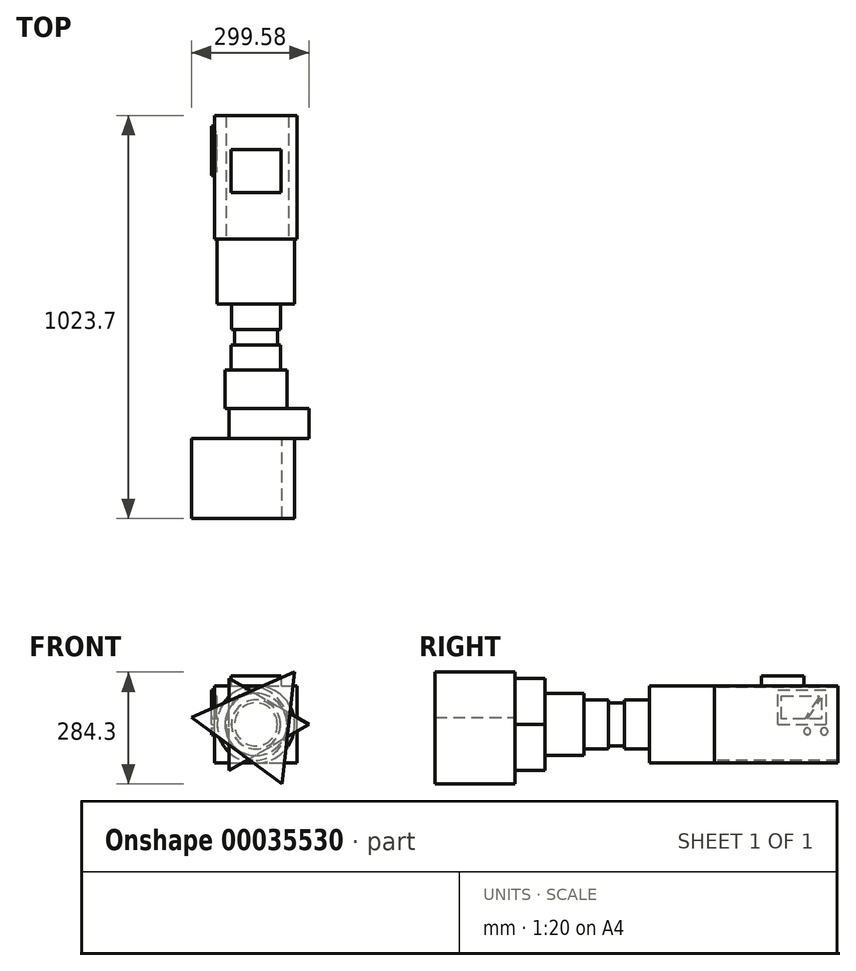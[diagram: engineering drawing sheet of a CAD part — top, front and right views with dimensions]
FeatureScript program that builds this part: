
annotation { "Feature Type Name" : "Feature", "Feature Type Description" : "" }
export const myFeature = defineFeature(function(context is Context, id is Id, definition is map)
    precondition{}
    {
        {
            var Q0;
            Q0=qCreatedBy(makeId("Front.planeOp"),FACE);
            var sketch = newSketch(context, id + "F0", { "sketchPlane" : qUnion([Q0])});
            skCircle(sketch, "E0", {"center": v(0, 0) * mm, "radius": 62.51 * mm});
            skSolve(sketch);
        }
        {
            var Q0;
            Q0=makeQuery(id+"F0.imprint","IMPRINT",FACE,{"disambiguationData":[TD([[makeQuery(id+"F0.imprint","IMPRINT",EDGE,{"derivedFrom":sQuery(id+"F0.wireOp",EDGE,"E0")}),1.0]])]});
            extrude(context, id + "F1", {"entities" : qUnion([Q0]), "depth" : 93.62 * mm, "hasSecondDirection" : true, "secondDirectionOppositeDirection" : true, "secondDirectionDepth" : 67.67 * mm});
        }
        {
            var Q0;
            Q0=makeQuery(id+"F1.opExtrude","CAP_FACE",FACE,{"disambiguationData":[OSD([sQuery(id+"F0.wireOp",EDGE,"E0")])],"isStart":false});
            var sketch = newSketch(context, id + "F2", { "sketchPlane" : qUnion([Q0])});
            skCircle(sketch, "E1", {"center": v(0, 0) * mm, "radius": 78.95 * mm});
            skSolve(sketch);
        }
        {
            var Q0;
            Q0 = qSketchRegion(id + "F2", true);
            extrude(context, id + "F3", {"entities" : qUnion([Q0]), "operationType" : NewBodyOperationType.ADD, "oppositeDirection" : true, "depth" : 97.99 * mm});
        }
        {
            var Q0;
            Q0=makeQuery(id+"F1.opExtrude","CAP_FACE",FACE,{"disambiguationData":[OSD([sQuery(id+"F0.wireOp",EDGE,"E0")])],"isStart":true});
            var sketch = newSketch(context, id + "F4", { "sketchPlane" : qUnion([Q0])});
            skCircle(sketch, "E2", {"center": v(0, 0) * mm, "radius": 54.56 * mm});
            skSolve(sketch);
        }
        {
            var Q0;
            Q0 = qSketchRegion(id + "F4", true);
            extrude(context, id + "F5", {"entities" : qUnion([Q0]), "operationType" : NewBodyOperationType.ADD, "depth" : 40.02 * mm});
        }
        {
            var Q0;
            Q0=makeQuery(id+"F5.opExtrude","CAP_FACE",FACE,{"disambiguationData":[OSD([sQuery(id+"F4.wireOp",EDGE,"E2")])],"isStart":false});
            var sketch = newSketch(context, id + "F6", { "sketchPlane" : qUnion([Q0])});
            skCircle(sketch, "E3", {"center": v(0, 0) * mm, "radius": 62.09 * mm});
            skSolve(sketch);
        }
        {
            var Q0;
            Q0 = qSketchRegion(id + "F6", true);
            extrude(context, id + "F7", {"entities" : qUnion([Q0]), "operationType" : NewBodyOperationType.ADD, "depth" : 64.06 * mm});
        }
        {
            var Q0;
            Q0=makeQuery(id+"F7.opExtrude","CAP_FACE",FACE,{"disambiguationData":[OSD([sQuery(id+"F6.wireOp",EDGE,"E3")])],"isStart":false});
            var sketch = newSketch(context, id + "F8", { "sketchPlane" : qUnion([Q0])});
            skCircle(sketch, "E4", {"center": v(0, 0) * mm, "radius": 98.34 * mm});
            skSolve(sketch);
        }
        {
            var Q0;
            Q0 = qSketchRegion(id + "F8", true);
            extrude(context, id + "F9", {"entities" : qUnion([Q0]), "operationType" : NewBodyOperationType.ADD, "depth" : 164.96 * mm});
        }
        {
            var Q0;
            Q0=makeQuery(id+"F9.opExtrude","CAP_FACE",FACE,{"disambiguationData":[OSD([sQuery(id+"F8.wireOp",EDGE,"E4")])],"isStart":false});
            var sketch = newSketch(context, id + "F10", { "sketchPlane" : qUnion([Q0])});
            skLineSegment(sketch, "E5.bottom", {"start": v(0, 0) * mm, "end": v(-104.59, 0) * mm});
            skLineSegment(sketch, "E5.top", {"start": v(0, 98.34) * mm, "end": v(-104.59, 98.34) * mm});
            skLineSegment(sketch, "E5.left", {"start": v(0, 0) * mm, "end": v(0, 98.34) * mm});
            skLineSegment(sketch, "E5.right", {"start": v(-104.59, 0) * mm, "end": v(-104.59, 98.34) * mm});
            skLineSegment(sketch, "E6.MirrorCS", {"start": v(0, 98.34) * mm, "end": v(104.59, 98.34) * mm});
            skLineSegment(sketch, "E7.MirrorCS", {"start": v(104.59, 0) * mm, "end": v(104.59, 98.34) * mm});
            skLineSegment(sketch, "E8.MirrorCS", {"start": v(0, 0) * mm, "end": v(104.59, 0) * mm});
            skLineSegment(sketch, "E9.MirrorCS", {"start": v(-104.59, 0) * mm, "end": v(-104.59, -98.34) * mm});
            skLineSegment(sketch, "E10.MirrorCS", {"start": v(0, -98.34) * mm, "end": v(-104.59, -98.34) * mm});
            skLineSegment(sketch, "E11.MirrorCS", {"start": v(0, 0) * mm, "end": v(0, -98.34) * mm});
            skLineSegment(sketch, "E12.MirrorCS", {"start": v(0, -98.34) * mm, "end": v(104.59, -98.34) * mm});
            skLineSegment(sketch, "E13.MirrorCS", {"start": v(104.59, 0) * mm, "end": v(104.59, -98.34) * mm});
            skFitSpline(sketch, "E14", {"points": [v(-83.55, 0) * mm, v(0, 94.29) * mm, v(75.89, 0) * mm, v(0, -91.4) * mm, v(-83.55, 0) * mm]});
            skSolve(sketch);
        }
        {
            var Q0;
            Q0 = qSketchRegion(id + "F10", true);
            extrude(context, id + "F11", {"entities" : qUnion([Q0]), "operationType" : NewBodyOperationType.ADD, "depth" : 313.97 * mm});
        }
        {
            var Q0;
            Q0=makeQuery(id+"F11.opExtrude","SWEPT_FACE",FACE,{"disambiguationData":[OSD([sQuery(id+"F10.wireOp",EDGE,"E5.top"),sQuery(id+"F10.wireOp",EDGE,"E6.MirrorCS")])]});
            var sketch = newSketch(context, id + "F12", { "sketchPlane" : qUnion([Q0])});
            skCircle(sketch, "E15.cCircle", {"center": v(0, 509.8) * mm, "radius": 87.57 * mm, "construction": true});
            skLineSegment(sketch, "E15.0", {"start": v(-86.16, 562.73) * mm, "end": v(2.77, 610.88) * mm});
            skLineSegment(sketch, "E15.1", {"start": v(2.77, 610.88) * mm, "end": v(88.92, 557.94) * mm});
            skLineSegment(sketch, "E15.2", {"start": v(88.92, 557.94) * mm, "end": v(86.16, 456.86) * mm});
            skLineSegment(sketch, "E15.3", {"start": v(86.16, 456.86) * mm, "end": v(-2.77, 408.7) * mm});
            skLineSegment(sketch, "E15.4", {"start": v(-2.77, 408.7) * mm, "end": v(-88.92, 461.64) * mm});
            skLineSegment(sketch, "E15.5", {"start": v(-88.92, 461.64) * mm, "end": v(-86.16, 562.73) * mm});
            skPoint(sketch, "E15.0.midPoint", {"position": v(-41.7, 586.8) * mm});
            skLineSegment(sketch, "E16.bottom", {"start": v(0, 509.8) * mm, "end": v(63.62, 509.8) * mm});
            skLineSegment(sketch, "E16.top", {"start": v(0, 564.12) * mm, "end": v(63.62, 564.12) * mm});
            skLineSegment(sketch, "E16.left", {"start": v(0, 509.8) * mm, "end": v(0, 564.12) * mm});
            skLineSegment(sketch, "E16.right", {"start": v(63.62, 509.8) * mm, "end": v(63.62, 564.12) * mm});
            skLineSegment(sketch, "E17.MirrorCS", {"start": v(0, 564.12) * mm, "end": v(-63.62, 564.12) * mm});
            skLineSegment(sketch, "E18.MirrorCS", {"start": v(-63.62, 509.8) * mm, "end": v(-63.62, 564.12) * mm});
            skLineSegment(sketch, "E19.MirrorCS", {"start": v(0, 509.8) * mm, "end": v(-63.62, 509.8) * mm});
            skLineSegment(sketch, "E20.MirrorCS", {"start": v(63.62, 509.8) * mm, "end": v(63.62, 455.46) * mm});
            skLineSegment(sketch, "E21.MirrorCS", {"start": v(0, 455.46) * mm, "end": v(63.62, 455.46) * mm});
            skLineSegment(sketch, "E22.MirrorCS", {"start": v(0, 509.8) * mm, "end": v(0, 455.46) * mm});
            skLineSegment(sketch, "E23.MirrorCS", {"start": v(-63.62, 509.8) * mm, "end": v(-63.62, 455.46) * mm});
            skLineSegment(sketch, "E24.MirrorCS", {"start": v(0, 455.46) * mm, "end": v(-63.62, 455.46) * mm});
            skSolve(sketch);
        }
        {
            var Q0;
            Q0=makeQuery(id+"F12.imprint","IMPRINT",FACE,{"disambiguationData":[TD([[makeQuery(id+"F12.imprint","IMPRINT",EDGE,{"derivedFrom":sQuery(id+"F12.wireOp",EDGE,"E16.bottom")}),1.0]])]});
            var Q1;
            Q1=makeQuery(id+"F12.imprint","IMPRINT",FACE,{"disambiguationData":[TD([[makeQuery(id+"F12.imprint","IMPRINT",EDGE,{"derivedFrom":sQuery(id+"F12.wireOp",EDGE,"E16.left")}),1.0]])]});
            var Q2;
            Q2=makeQuery(id+"F12.imprint","IMPRINT",FACE,{"disambiguationData":[TD([[makeQuery(id+"F12.imprint","IMPRINT",EDGE,{"derivedFrom":sQuery(id+"F12.wireOp",EDGE,"E16.bottom")}),-1.0]])]});
            var Q3;
            Q3=makeQuery(id+"F12.imprint","IMPRINT",FACE,{"disambiguationData":[TD([[makeQuery(id+"F12.imprint","IMPRINT",EDGE,{"derivedFrom":sQuery(id+"F12.wireOp",EDGE,"E22.MirrorCS")}),-1.0]])]});
            extrude(context, id + "F13", {"entities" : qUnion([Q0, Q1, Q2, Q3]), "operationType" : NewBodyOperationType.ADD, "depth" : 25.4 * mm});
        }
        {
            var Q0;
            Q0=makeQuery(id+"F3.boolean.opBoolean","MERGE",FACE,{"derivedFrom":[makeQuery(id+"F1.opExtrude","CAP_FACE",FACE,{"disambiguationData":[OSD([sQuery(id+"F0.wireOp",EDGE,"E0")])],"isStart":false}),makeQuery(id+"F3.opExtrude","CAP_FACE",FACE,{"disambiguationData":[OSD([sQuery(id+"F2.wireOp",EDGE,"E1")])],"isStart":true})]});
            var sketch = newSketch(context, id + "F14", { "sketchPlane" : qUnion([Q0])});
            skCircle(sketch, "E25.cCircle", {"center": v(0, 0) * mm, "radius": 67.72 * mm, "construction": true});
            skLineSegment(sketch, "E25.0", {"start": v(-67.72, -117.3) * mm, "end": v(-67.72, 117.3) * mm});
            skLineSegment(sketch, "E25.1", {"start": v(-67.72, 117.3) * mm, "end": v(135.44, 0) * mm});
            skLineSegment(sketch, "E25.2", {"start": v(135.44, 0) * mm, "end": v(-67.72, -117.3) * mm});
            skPoint(sketch, "E25.0.midPoint", {"position": v(-67.72, 0) * mm});
            skSolve(sketch);
        }
        {
            var Q0;
            Q0 = qSketchRegion(id + "F14", true);
            extrude(context, id + "F15", {"entities" : qUnion([Q0]), "operationType" : NewBodyOperationType.ADD, "depth" : 76.2 * mm});
        }
        {
            var Q0;
            Q0=makeQuery(id+"F15.opExtrude","CAP_FACE",FACE,{"disambiguationData":[OSD([sQuery(id+"F14.wireOp",EDGE,"E25.0"),sQuery(id+"F14.wireOp",EDGE,"E25.1"),sQuery(id+"F14.wireOp",EDGE,"E25.2")])],"isStart":false});
            var sketch = newSketch(context, id + "F16", { "sketchPlane" : qUnion([Q0])});
            skCircle(sketch, "E26.cCircle", {"center": v(0, 0) * mm, "radius": 82.55 * mm, "construction": true});
            skLineSegment(sketch, "E26.0", {"start": v(-164.14, 17.88) * mm, "end": v(97.55, 133.2) * mm});
            skLineSegment(sketch, "E26.1", {"start": v(97.55, 133.2) * mm, "end": v(66.58, -151.09) * mm});
            skLineSegment(sketch, "E26.2", {"start": v(66.58, -151.09) * mm, "end": v(-164.14, 17.88) * mm});
            skPoint(sketch, "E26.0.midPoint", {"position": v(-33.3, 75.54) * mm});
            skSolve(sketch);
        }
        {
            var Q0;
            Q0 = qSketchRegion(id + "F16", true);
            extrude(context, id + "F17", {"entities" : qUnion([Q0]), "operationType" : NewBodyOperationType.ADD, "depth" : 203.2 * mm});
        }
        {
            var Q0;
            Q0=makeQuery(id+"F11.opExtrude","SWEPT_FACE",FACE,{"disambiguationData":[OSD([sQuery(id+"F10.wireOp",EDGE,"E7.MirrorCS"),sQuery(id+"F10.wireOp",EDGE,"E13.MirrorCS")])]});
            var sketch = newSketch(context, id + "F18", { "sketchPlane" : qUnion([Q0])});
            skLineSegment(sketch, "E27.bottom", {"start": v(-497.98, 0) * mm, "end": v(-621.23, 0) * mm});
            skLineSegment(sketch, "E27.top", {"start": v(-497.98, 87.36) * mm, "end": v(-621.23, 87.36) * mm});
            skLineSegment(sketch, "E27.left", {"start": v(-497.98, 0) * mm, "end": v(-497.98, 87.36) * mm});
            skLineSegment(sketch, "E27.right", {"start": v(-621.23, 0) * mm, "end": v(-621.23, 87.36) * mm});
            skCircle(sketch, "E28", {"center": v(-615.3, -17.65) * mm, "radius": 9.08 * mm});
            skLineSegment(sketch, "E29", {"start": v(-615.3, -17.65) * mm, "end": v(-572.3, -17.65) * mm});
            skCircle(sketch, "E30", {"center": v(-572.3, -17.65) * mm, "radius": 8.4 * mm});
            skCircle(sketch, "E31", {"center": v(-616.24, -40.2) * mm, "radius": 4.72 * mm});
            skSolve(sketch);
        }
        {
            var Q0;
            Q0=makeQuery(id+"F18.imprint","IMPRINT",FACE,{"disambiguationData":[TD([[makeQuery(id+"F18.imprint","IMPRINT",EDGE,{"derivedFrom":sQuery(id+"F18.wireOp",EDGE,"E27.bottom")}),1.0]])]});
            var sketch = newSketch(context, id + "F19", { "sketchPlane" : qUnion([Q0])});
            skSolve(sketch);
        }
        {
            var Q0;
            Q0 = qSketchRegion(id + "F19", true);
            var Q1;
            Q1=makeQuery(id+"F18.imprint","IMPRINT",FACE,{"disambiguationData":[TD([[makeQuery(id+"F18.imprint","IMPRINT",EDGE,{"derivedFrom":sQuery(id+"F18.wireOp",EDGE,"E27.bottom")}),-1.0]])]});
            var Q2;
            Q2=makeQuery(id+"F18.imprint","IMPRINT",FACE,{"disambiguationData":[TD([[makeQuery(id+"F18.imprint","IMPRINT",EDGE,{"derivedFrom":sQuery(id+"F18.wireOp",EDGE,"E28")}),1.0]])]});
            var Q3;
            Q3=makeQuery(id+"F18.imprint","IMPRINT",FACE,{"disambiguationData":[TD([[makeQuery(id+"F18.imprint","IMPRINT",EDGE,{"derivedFrom":sQuery(id+"F18.wireOp",EDGE,"E30")}),1.0]])]});
            extrude(context, id + "F20", {"entities" : qUnion([Q0, Q1, Q2, Q3]), "operationType" : NewBodyOperationType.ADD, "depth" : 7.62 * mm});
        }
        {
            var Q0;
            Q0=makeQuery(id+"F20.opExtrude","CAP_FACE",FACE,{"disambiguationData":[OSD([sQuery(id+"F18.wireOp",EDGE,"E27.bottom"),sQuery(id+"F18.wireOp",EDGE,"E27.top"),sQuery(id+"F18.wireOp",EDGE,"E27.left"),sQuery(id+"F18.wireOp",EDGE,"E27.right")])],"isStart":false});
            var sketch = newSketch(context, id + "F21", { "sketchPlane" : qUnion([Q0])});
            skLineSegment(sketch, "E32", {"start": v(-608.25, 67.2) * mm, "end": v(-608.25, 13.51) * mm});
            skLineSegment(sketch, "E33", {"start": v(-608.25, 13.51) * mm, "end": v(-572.84, 13.51) * mm});
            skLineSegment(sketch, "E34", {"start": v(-572.84, 13.51) * mm, "end": v(-608.25, 67.2) * mm});
            skLineSegment(sketch, "E35", {"start": v(-601.15, 67.61) * mm, "end": v(-565.96, 14.28) * mm});
            skLineSegment(sketch, "E36", {"start": v(-565.96, 14.28) * mm, "end": v(-506.72, 14.28) * mm});
            skLineSegment(sketch, "E37", {"start": v(-506.72, 14.28) * mm, "end": v(-506.72, 71.92) * mm});
            skLineSegment(sketch, "E38", {"start": v(-506.72, 71.92) * mm, "end": v(-601.25, 71.92) * mm});
            skLineSegment(sketch, "E39", {"start": v(-601.25, 71.92) * mm, "end": v(-601.15, 67.61) * mm});
            skSolve(sketch);
        }
        {
            var Q0;
            Q0=makeQuery(id+"F21.imprint","IMPRINT",FACE,{"disambiguationData":[TD([[makeQuery(id+"F21.imprint","IMPRINT",EDGE,{"derivedFrom":sQuery(id+"F21.wireOp",EDGE,"E32")}),1.0]])]});
            var Q1;
            Q1=makeQuery(id+"F21.imprint","IMPRINT",FACE,{"disambiguationData":[TD([[makeQuery(id+"F21.imprint","IMPRINT",EDGE,{"derivedFrom":sQuery(id+"F21.wireOp",EDGE,"E35")}),1.0]])]});
            extrude(context, id + "F22", {"entities" : qUnion([Q0, Q1]), "operationType" : NewBodyOperationType.REMOVE, "oppositeDirection" : true, "depth" : 12.18 * mm});
        }
    });
